# Revit family: Network Camera-ePTZ-Q-SYS-NC-90-G2
name_source: partatom
category: Communication Devices
units: mm (PartAtom-declared; Revit-internal decimal feet)

## family parameters
Cut with Voids When Loaded = No
Host = Face
Maintain Annotation Orientation = No
OmniClass Number = 23.85.10.14.11
OmniClass Title = Cameras
Part Type = Normal
Room Calculation Point = No
Round Connector Dimension = Use Diameter
Shared = No

## types (1)
- Black
    Assembly Code = E1020500
    Base 1 Width = 120 mm  [stored 0.393701 ft]
    Base Height = 100 mm  [stored 0.328084 ft]
    Body Material = Paint - Q-SYS - Black
    Body Radius 1 = 126 mm
    Body Radius 2 = 93 mm  [stored 0.305118 ft]
    Camera Front to Center = 73 mm  [stored 0.239501 ft]
    Camera Half Height = 45 mm
    Camera Half Width = 40 mm  [stored 0.131234 ft]
    Coverage Vertical = 120.00°
    Default Elevation = 1219 mm
    Depth = 56 mm  [stored 0.183727 ft]
    Description = Network ePTZ conference camera
    Height = 106 mm  [stored 0.347769 ft]
    Highlight Material = Glass - Q-SYS - Lens
    IQ Category = Network Camera
    Length 1 = 8 mm  [stored 0.0262467 ft]
    Length 2 = 54 mm  [stored 0.177165 ft]
    Length 3 = 6 mm  [stored 0.019685 ft]
    Length 4 = 40 mm  [stored 0.131234 ft]
    Length 5 = 7 mm  [stored 0.0229659 ft]
    Length 6 = 120 mm  [stored 0.393701 ft]
    Length 7 = 110 mm
    Manufacturer = Q-SYS
    Manufacturer URL = https://www.qsys.com
    Model = NC-90-G2
    Offset = 279 mm
    OmniClass Number = 23.85.10.14.11
    Part Number = NC-90-G2
    Product Documentation Link = https://www.qsys.com
    Product Page URL = https://www.qsys.com
    Type Comments = Black
    URL = https://www.qsys.com
    Voltage DC = PoE (Type 1)
    Weight = 1.50 lbm
    Weight Dimensional = 1.5
    Weight Product = 1.5
    Width = 253 mm

note: [stored X ft] marks values corroborated as IEEE doubles in the binary element streams (Revit-internal decimal feet)

## geometry (parser evidence)
native form markers: Sweep x5
no freeform markers — native parametric forms only
